# Revit family: CADS_AIRFLOWdev_AirTerminal_RoofCowl_Exhaust
name_source: partatom
category: Air Terminals
revit_build: Autodesk Revit 2015 (Build: 20160512_0715(x64)
units: mm (PartAtom-declared; Revit-internal decimal feet)

## types (1)
- Grey Roof Cowl
    6MonthlyMaintenance = Visually inspect system, clean the fan and ducting if necessary
    A = 200 mm  [stored 0.656168 ft]
    AirflowRateRange = 0-61
    AssetType = Fixed
    CEApproval = Yes
    Color = Grey
    Constituents = Grey
    Default Elevation = 1219 mm
    Description = Roof Cowl Grey A.B.S.
    DurationUnit = Years
    Exclusions = Incorrect Use / Incorrect Installation / Installed by a non-accredited electrician. Customer abuse.
    FaceType = LOUVERED
    FlowControlType = NONE
    GlobalTradeItemNumber = 5019009310442
    Grade = Virgin
    GrossWeight = 0.02 kg
    HasIntegralControl = No
    HasSoundAttenuator = No
    HasThermalInsulation = No
    ISO140001 = Yes
    ISO90001 = Yes
    IsExtendedWarranty = No
    Manufacturer = Airflow Developments Ltd
    ManufacturerAddress = Aidelle House
Lancaster Road
Cressex Business Park
High Wycombe
Bucks
HP123QP
    ManufacturerTelephone = 01494 525252
    ManufacturerWebsite = www.airflow.com
    Material = Plastic
    ModelLabel = Roof Cowl Grey A.B.S.
    ModelReference = 9004554
    MountingType = SURFACE
    NBSCode = 90-75-50/370 Air terminals;
    NominalHeight = 117 mm  [stored 0.383858 ft]
    NominalLength = 125 mm  [stored 0.410105 ft]
    NominalWidth = 117 mm  [stored 0.383858 ft]
    NumberOfSlots = 0
    PointOfContact = Airflow Developments Ltd
    ProductionYear = 2017
    ReplacementCost = 39.336
    RoofCowl = CADS_AirFlow_White
    ServiceLifeDuration = 10
    ServiceLifeType = EXPECTEDSERVICELIFE
    Shape = Round
    ShippingWeight = 0.02 kg
    Size = 125 x 117 x 117
    Uniclass2015 = Pr_65_70_46_01
    WarrantyContent = Replacement of part if faulty
    WarrantyGuarantor = Airflow Developments Ltd
    WarrantyPeriod = 2

note: [stored X ft] marks values corroborated as IEEE doubles in the binary element streams (Revit-internal decimal feet)

## geometry (parser evidence)
native form markers: Sweep x2
no freeform markers — native parametric forms only
